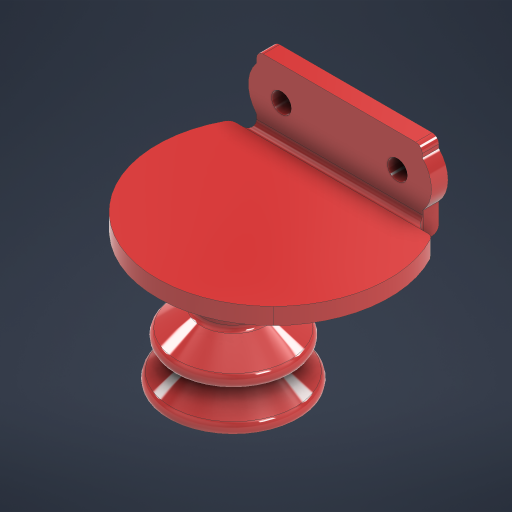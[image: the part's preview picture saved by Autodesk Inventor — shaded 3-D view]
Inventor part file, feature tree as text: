
AUTODESK INVENTOR PART (.ipt)
format: ipt  version: 2024.1 (Build 281209000, 209)  size: 376,832 bytes
history: native  units: in
note: dims shown in document units (in); Inventor stores cm internally (conversion verified against a paired STEP export)
features: extrude x2, fillet x2, sketch x2, projected_geometry x2, imported_body x1, direct_edit x1, other x1
ambient origin geometry x8: Origin, YZ Plane, XZ Plane, XY Plane, X Axis, Y Axis, Z Axis, Center Point
bodies: Solid1 (feature_tree)
feature tree (11):
  imported_body  "Base1"
  direct_edit  "Direct Edit1"
  extrude  "Extrusion1"  Depth=0.3937in TaperAngle=0.0deg
  extrude  "Extrusion2"  Depth=1.9685in
  fillet  "Fillet1"  Radius=1.9685in
  fillet  "Fillet2"  [1 undecoded]
  sketch  "Sketch1"  dims[d0=8.7082in d1=0.3937in d2=0.3937in d3=0.3937in d4=0.0in]
  projected_geometry  "Projected Loop1"
  sketch  "Sketch2"  dims[d5=0.3937in d6=0.0in d7=1.9685in d8=1.9685in]
  projected_geometry  "Projected Loop2"
  other  "Scale1"
note: 1 required parameter value undecoded (feature->parameter linkage not recoverable at this tier; creation-order binding heuristic only, values carry confidence <= 0.55)
